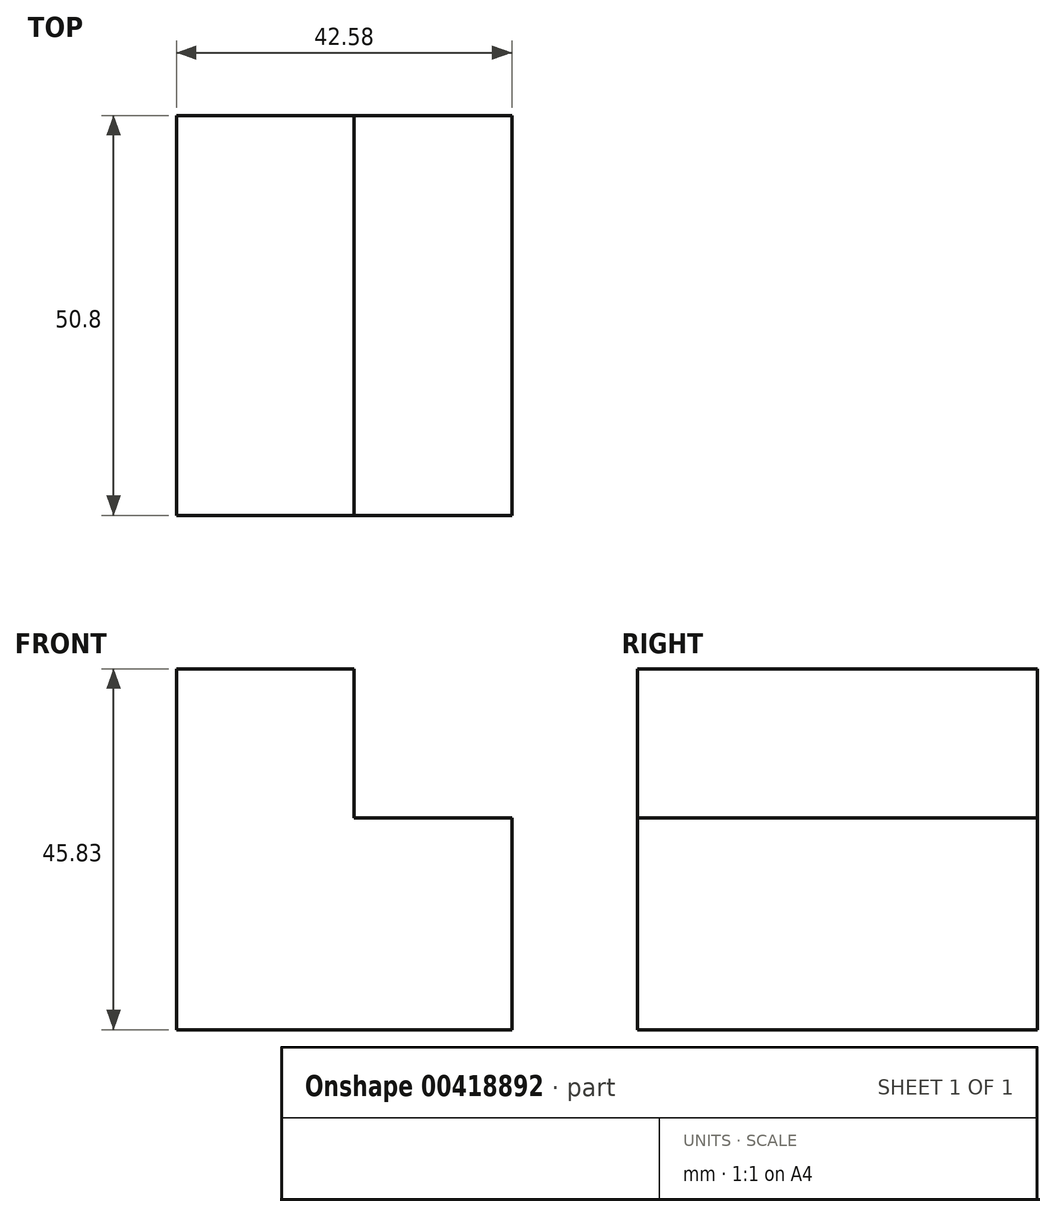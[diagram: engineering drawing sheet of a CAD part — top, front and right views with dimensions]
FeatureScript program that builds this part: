
annotation { "Feature Type Name" : "Feature", "Feature Type Description" : "" }
export const myFeature = defineFeature(function(context is Context, id is Id, definition is map)
    precondition{}
    {
        {
            var Q0;
            Q0=qCreatedBy(makeId("Front.planeOp"),FACE);
            var sketch = newSketch(context, id + "F0", { "sketchPlane" : qUnion([Q0])});
            skLineSegment(sketch, "E0", {"start": v(0, 0) * mm, "end": v(-42.58, 0) * mm});
            skLineSegment(sketch, "E1", {"start": v(-42.58, 0) * mm, "end": v(-42.58, 45.83) * mm});
            skLineSegment(sketch, "E2", {"start": v(-42.58, 45.83) * mm, "end": v(-20.05, 45.83) * mm});
            skLineSegment(sketch, "E3", {"start": v(-20.05, 45.83) * mm, "end": v(-20.05, 26.92) * mm});
            skLineSegment(sketch, "E4", {"start": v(-20.05, 26.92) * mm, "end": v(0, 26.92) * mm});
            skLineSegment(sketch, "E5", {"start": v(0, 26.92) * mm, "end": v(0, 0) * mm});
            skSolve(sketch);
        }
        {
            var Q0;
            Q0 = qSketchRegion(id + "F0", true);
            extrude(context, id + "F1", {"entities" : qUnion([Q0]), "depth" : 50.8 * mm});
        }
    });
